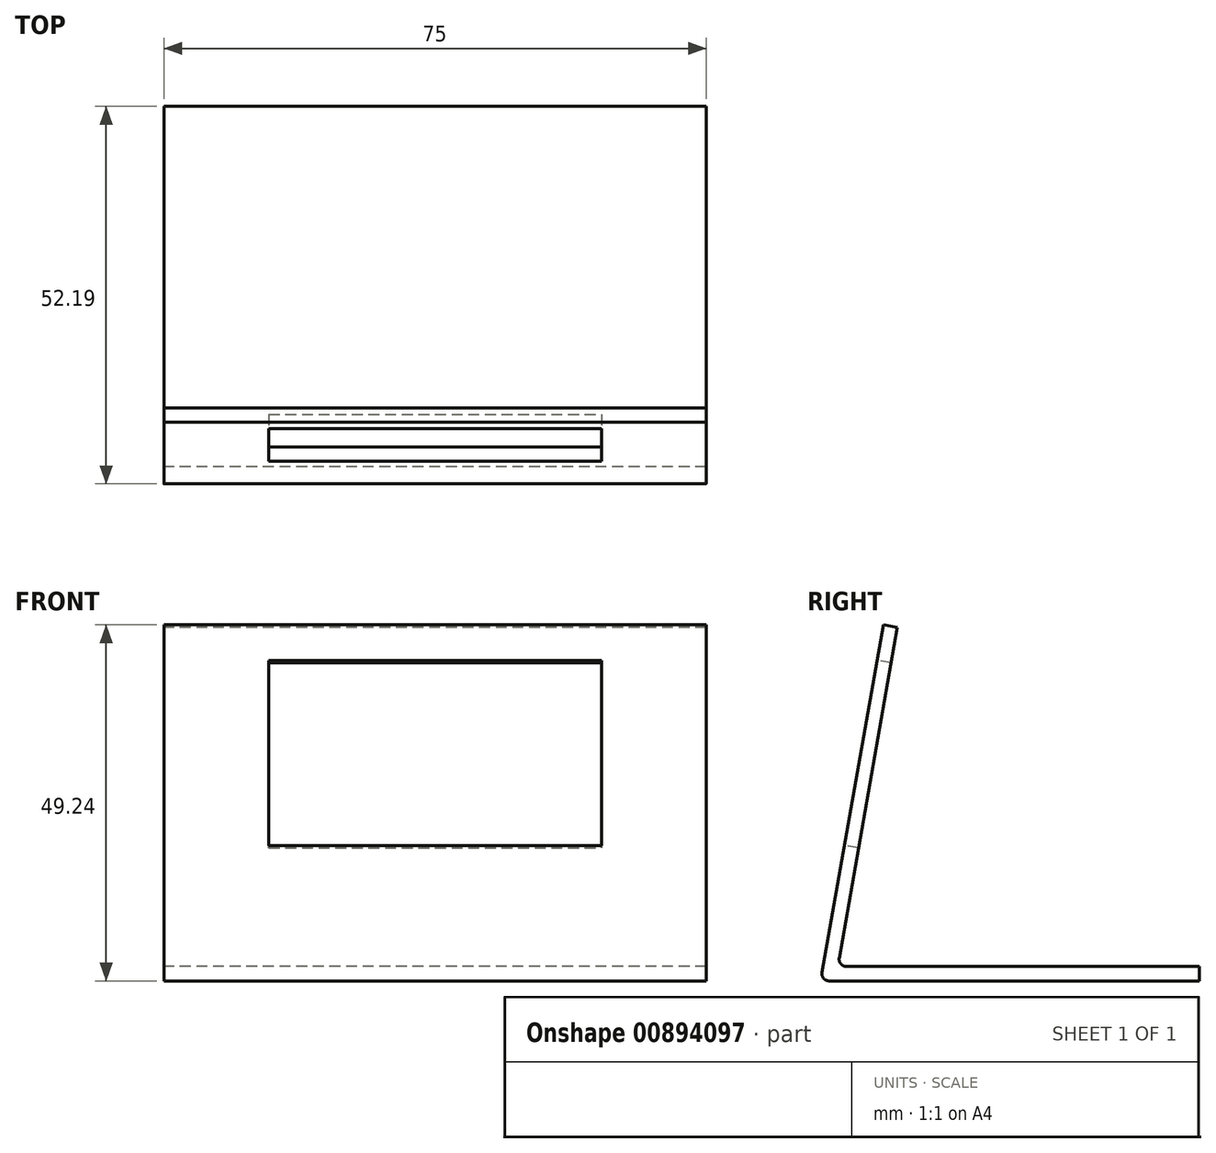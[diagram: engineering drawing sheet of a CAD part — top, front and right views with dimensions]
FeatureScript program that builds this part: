
annotation { "Feature Type Name" : "Feature", "Feature Type Description" : "" }
export const myFeature = defineFeature(function(context is Context, id is Id, definition is map)
    precondition{}
    {
        {
            var Q0;
            Q0=qCreatedBy(makeId("Right.planeOp"),FACE);
            var sketch = newSketch(context, id + "F0", { "sketchPlane" : qUnion([Q0])});
            skLineSegment(sketch, "E0", {"start": v(0, 0) * mm, "end": v(-48.8, 0) * mm});
            skLineSegment(sketch, "E1", {"start": v(-49.8, 1.17) * mm, "end": v(-41.73, 46.9) * mm});
            skLineSegment(sketch, "E2.0", {"start": v(-52.18, -0.83) * mm, "end": v(-43.7, 47.24) * mm});
            skLineSegment(sketch, "E2.1", {"start": v(0, -2) * mm, "end": v(-51.2, -2) * mm});
            skLineSegment(sketch, "E3", {"start": v(-43.7, 47.24) * mm, "end": v(-41.73, 46.9) * mm});
            skLineSegment(sketch, "E4", {"start": v(0, 0) * mm, "end": v(0, -2) * mm});
            skPoint(sketch, "E5.visualSharp", {"position": v(-52.38, -2) * mm});
            skArc(sketch, "E5.filletArc", {"start": v(-52.18, -0.83) * mm, "mid": v(-51.96, -1.64) * mm, "end": v(-51.2, -2) * mm});
            skPoint(sketch, "E6.visualSharp", {"position": v(-50, 0) * mm});
            skArc(sketch, "E6.filletArc", {"start": v(-49.8, 1.17) * mm, "mid": v(-49.57, 0.36) * mm, "end": v(-48.8, 0) * mm});
            skSolve(sketch);
        }
        {
            var Q0;
            Q0 = qSketchRegion(id + "F0", true);
            extrude(context, id + "F1", {"entities" : qUnion([Q0]), "depth" : 75 * mm, "offsetDistance" : 25 * mm});
        }
        {
            var Q0;
            Q0=makeQuery(id+"F1.opExtrude","SWEPT_FACE",FACE,{"disambiguationData":[OSD([sQuery(id+"F0.wireOp",EDGE,"E2.0")])]});
            var sketch = newSketch(context, id + "F2", { "sketchPlane" : qUnion([Q0])});
            skLineSegment(sketch, "E7.0.0", {"start": v(0, 38.93) * mm, "end": v(0, -9.87) * mm});
            skLineSegment(sketch, "E7.0.1", {"start": v(0, -9.87) * mm, "end": v(75, -9.87) * mm});
            skLineSegment(sketch, "E7.0.2", {"start": v(75, -9.87) * mm, "end": v(75, 38.93) * mm});
            skLineSegment(sketch, "E7.0.3", {"start": v(75, 38.93) * mm, "end": v(0, 38.93) * mm});
            skLineSegment(sketch, "E8.bottom", {"start": v(60.5, 7.93) * mm, "end": v(14.5, 7.93) * mm});
            skLineSegment(sketch, "E8.top", {"start": v(60.5, 33.93) * mm, "end": v(14.5, 33.93) * mm});
            skLineSegment(sketch, "E8.left", {"start": v(60.5, 7.93) * mm, "end": v(60.5, 33.93) * mm});
            skLineSegment(sketch, "E8.right", {"start": v(14.5, 7.93) * mm, "end": v(14.5, 33.93) * mm});
            skPoint(sketch, "E8.middle", {"position": v(37.5, 20.93) * mm});
            skPoint(sketch, "E8.middle.positionSnap0", {"position": v(37.5, 38.93) * mm});
            skPoint(sketch, "E8.centerSnap0", {"position": v(37.5, 38.93) * mm});
            skSolve(sketch);
        }
        {
            var Q0;
            Q0=makeQuery(id+"F2.imprint","IMPRINT",FACE,{"disambiguationData":[TD([[makeQuery(id+"F2.imprint","IMPRINT",EDGE,{"derivedFrom":sQuery(id+"F2.wireOp",EDGE,"E8.bottom")}),-1.0]])]});
            var Q1;
            Q1=makeQuery(id+"F1.opExtrude","SWEPT_FACE",FACE,{"disambiguationData":[OSD([sQuery(id+"F0.wireOp",EDGE,"E1")])]});
            extrude(context, id + "F3", {"entities" : qUnion([Q0]), "operationType" : NewBodyOperationType.REMOVE, "endBound" : BoundingType.UP_TO_SURFACE, "oppositeDirection" : true, "depth" : 25 * mm, "endBoundEntityFace" : qUnion([Q1]), "offsetDistance" : 25 * mm});
        }
    });
